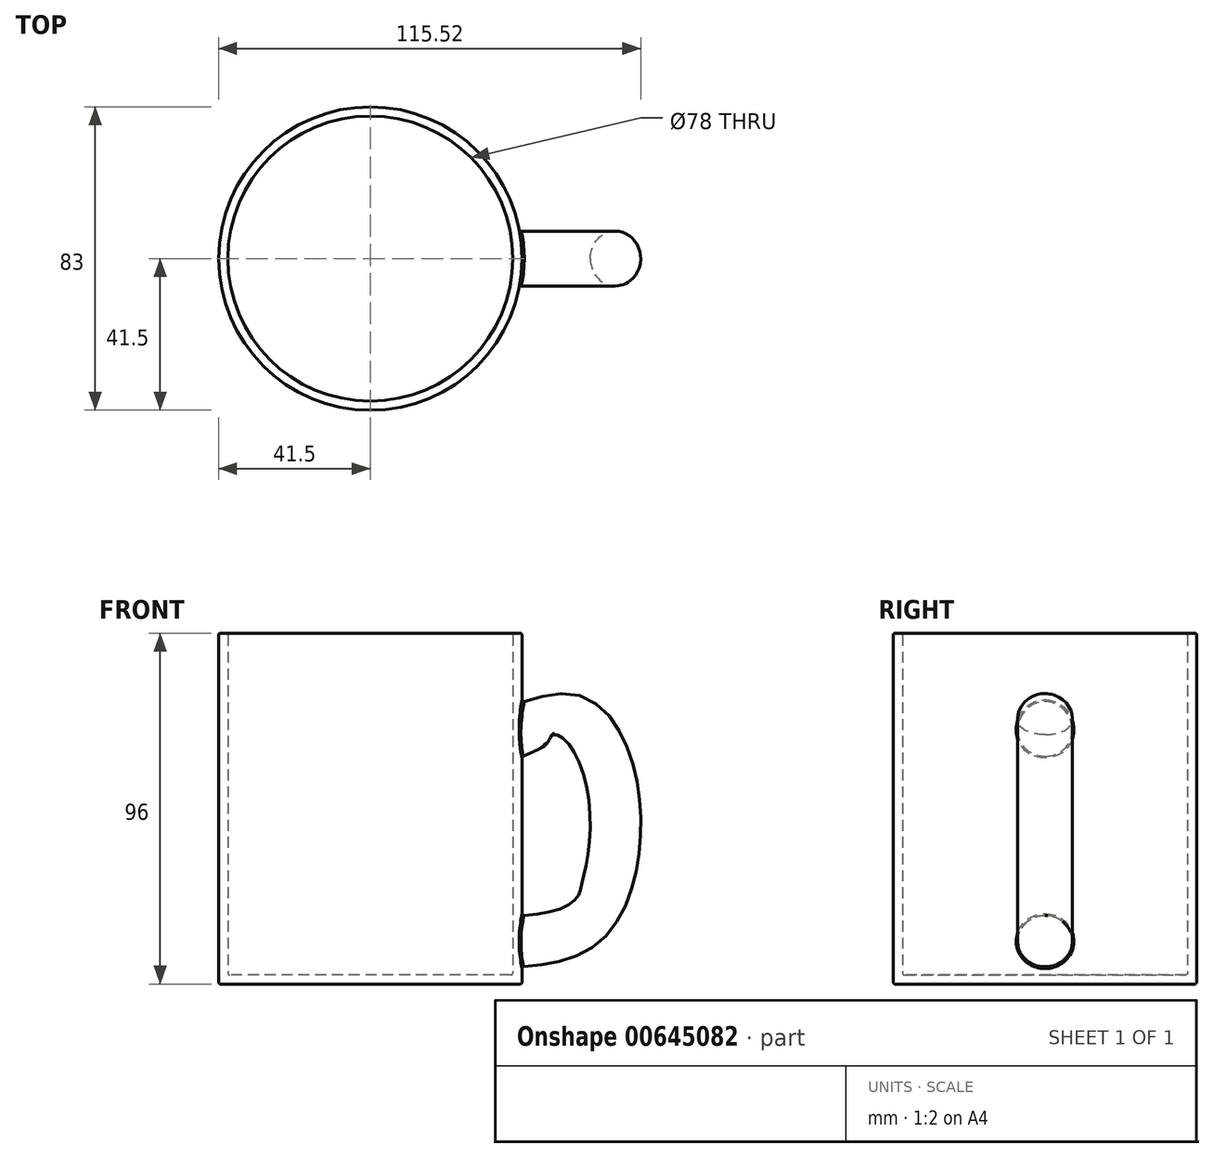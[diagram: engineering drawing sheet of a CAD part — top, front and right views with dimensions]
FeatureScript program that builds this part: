
annotation { "Feature Type Name" : "Feature", "Feature Type Description" : "" }
export const myFeature = defineFeature(function(context is Context, id is Id, definition is map)
    precondition{}
    {
        {
            var Q0;
            Q0=qCreatedBy(makeId("Top.planeOp"),FACE);
            var sketch = newSketch(context, id + "F0", { "sketchPlane" : qUnion([Q0])});
            skCircle(sketch, "E0", {"center": v(0, 0) * mm, "radius": 41.5 * mm});
            skSolve(sketch);
        }
        {
            var Q0;
            Q0 = qSketchRegion(id + "F0", true);
            extrude(context, id + "F1", {"entities" : qUnion([Q0]), "depth" : 96 * mm, "offsetDistance" : 25 * mm});
        }
        {
            var Q0;
            Q0=qCreatedBy(makeId("Front.planeOp"),FACE);
            var sketch = newSketch(context, id + "F2", { "sketchPlane" : qUnion([Q0])});
            skFitSpline(sketch, "E1", {"points": [v(35.19, 73.34) * mm, v(57.97, 77.36) * mm, v(72.06, 53.42) * mm, v(63.44, 13.84) * mm, v(34.4, 5.46) * mm], "startDerivative": vector(111.4, 44.36) * mm, "endDerivative": vector(-131.93, -7.13) * mm});
            skSolve(sketch);
        }
        {
            var Q0;
            Q0=qCreatedBy(makeId("Right.planeOp"),FACE);
            cPlane(context, id + "F3", {"entities" : qUnion([Q0]), "cplaneType" : CPlaneType.OFFSET, "offset" : 39.6 * mm, "width" : 150 * mm, "height" : 150 * mm});
        }
        {
            var Q0;
            Q0=qCreatedBy(id+"F3.planeOp",FACE);
            var sketch = newSketch(context, id + "F4", { "sketchPlane" : qUnion([Q0])});
            skCircle(sketch, "E2", {"center": v(0, 68.89) * mm, "radius": 7.5 * mm});
            skSolve(sketch);
        }
        {
            var Q0;
            Q0 = qSketchRegion(id + "F4", true);
            var Q1;
            Q1 = qConstructionFilter(qBodyType(qCreatedBy(id + "F2" ,EDGE), BodyType.WIRE), ConstructionObject.NO);
            sweep(context, id + "F5", {"operationType" : NewBodyOperationType.ADD, "profiles" : qUnion([Q0]), "path" : qUnion([Q1])});
        }
        {
            var Q0;
            Q0=makeQuery(id+"F1.opExtrude","CAP_FACE",FACE,{"disambiguationData":[OSD([sQuery(id+"F0.wireOp",EDGE,"E0")])],"isStart":false});
            shell(context, id + "F6", {"entities" : qUnion([Q0]), "thickness" : 2.5 * mm});
        }
        {
            var Q0;
            {var subQ0=sQuery(id+"F0.wireOp",EDGE,"E0");Q0=makeQuery(id+"F6.opShell","OFFSET_FACE",FACE,{"disambiguationData":[OSD([subQ0]),TDD([makeQuery(id+"F1.opExtrude","SWEPT_FACE",FACE,{"disambiguationData":[OSD([subQ0])]})])]});}
            var Q1;
            Q1=makeQuery(id+"F1.opExtrude","SWEPT_FACE",FACE,{"disambiguationData":[OSD([sQuery(id+"F0.wireOp",EDGE,"E0")])]});
            fillet(context, id + "F7", {"entities" : qUnion([Q0, Q1]), "radius" : .5 * mm, "tangentPropagation" : true, "allowEdgeOverflow" : false});
        }
    });
